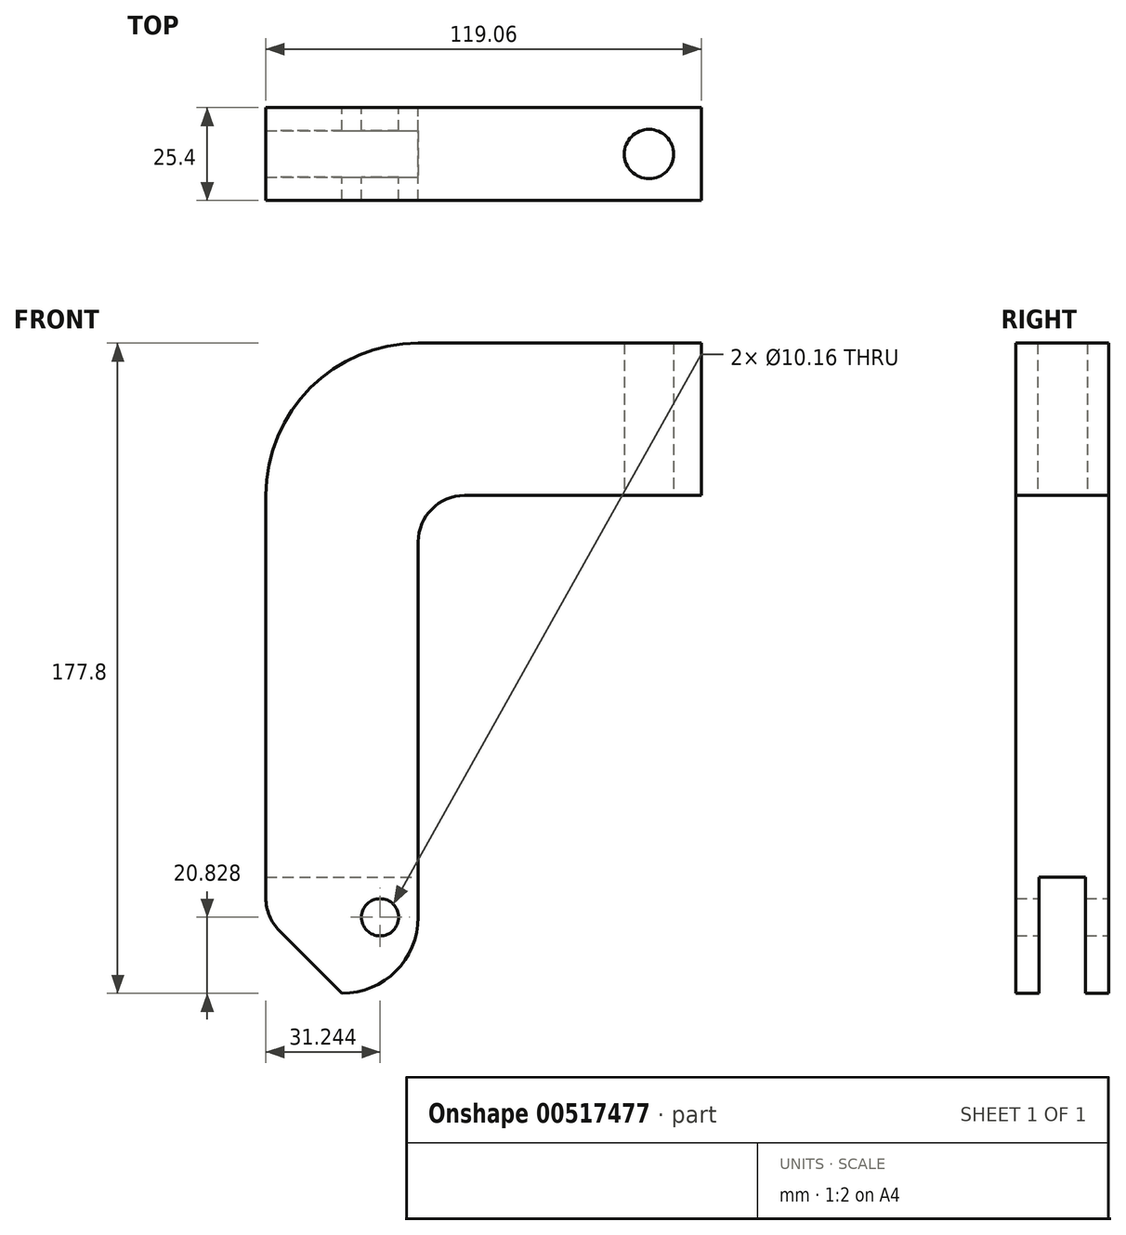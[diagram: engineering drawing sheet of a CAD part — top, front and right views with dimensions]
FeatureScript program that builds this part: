
annotation { "Feature Type Name" : "Feature", "Feature Type Description" : "" }
export const myFeature = defineFeature(function(context is Context, id is Id, definition is map)
    precondition{}
    {
        {
            var Q0;
            Q0=qCreatedBy(makeId("Front.planeOp"),FACE);
            var sketch = newSketch(context, id + "F0", { "sketchPlane" : qUnion([Q0])});
            skLineSegment(sketch, "E0.bottom", {"start": v(20.83, 88.9) * mm, "end": v(20.83, 88.9) * mm});
            skLineSegment(sketch, "E0.left", {"start": v(20.83, 34.54) * mm, "end": v(20.83, -68.07) * mm});
            skLineSegment(sketch, "E0.right", {"start": v(-20.83, 47.24) * mm, "end": v(-20.83, -62.81) * mm});
            skPoint(sketch, "E0.middle", {"position": v(0, 0) * mm});
            skPoint(sketch, "E1.visualSharp", {"position": v(-20.83, 88.9) * mm});
            skArc(sketch, "E1.filletArc", {"start": v(20.83, 88.9) * mm, "mid": v(-8.63, 76.7) * mm, "end": v(-20.83, 47.24) * mm});
            skLineSegment(sketch, "E2", {"start": v(0, -88.9) * mm, "end": v(-17.1, -71.8) * mm});
            skPoint(sketch, "E3.visualSharp", {"position": v(20.83, -88.9) * mm});
            skArc(sketch, "E3.filletArc", {"start": v(0, -88.9) * mm, "mid": v(14.73, -82.8) * mm, "end": v(20.83, -68.07) * mm});
            skPoint(sketch, "E0.top.end.orphan", {"position": v(-20.83, -88.9) * mm});
            skLineSegment(sketch, "E4", {"start": v(33.53, 47.24) * mm, "end": v(98.23, 47.24) * mm});
            skLineSegment(sketch, "E5", {"start": v(20.83, 88.9) * mm, "end": v(98.23, 88.9) * mm});
            skLineSegment(sketch, "E6", {"start": v(98.23, 88.9) * mm, "end": v(98.23, 47.24) * mm});
            skPoint(sketch, "E7.visualSharp", {"position": v(-20.83, -68.07) * mm});
            skArc(sketch, "E7.filletArc", {"start": v(-20.83, -62.81) * mm, "mid": v(-19.86, -67.67) * mm, "end": v(-17.1, -71.8) * mm});
            skArc(sketch, "E8.filletArc", {"start": v(33.53, 47.24) * mm, "mid": v(24.55, 43.52) * mm, "end": v(20.83, 34.54) * mm});
            skCircle(sketch, "E9", {"center": v(10.41, -68.07) * mm, "radius": 5.08 * mm});
            skPoint(sketch, "E10.end.orphan", {"position": v(15.5, -68.07) * mm});
            skSolve(sketch);
        }
        {
            var Q0;
            Q0 = qSketchRegion(id + "F0", true);
            extrude(context, id + "F1", {"entities" : qUnion([Q0]), "endBound" : BoundingType.SYMMETRIC, "depth" : 25.4 * mm, "offsetDistance" : 25.4 * mm});
        }
        {
            var Q0;
            Q0=qCreatedBy(makeId("Top.planeOp"),FACE);
            var sketch = newSketch(context, id + "F2", { "sketchPlane" : qUnion([Q0])});
            skPoint(sketch, "E11", {"position": v(83.95, 0) * mm});
            skSolve(sketch);
        }
        {
            var Q0;
            Q0=sQuery(id+"F2.wireOp",VERTEX,"E11");
            var Q1;
            Q1=makeQuery(id+"F1.opExtrude","SWEPT_BODY",BODY,{"disambiguationData":[OSD([sQuery(id+"F0.wireOp",EDGE,"E0.left"),sQuery(id+"F0.wireOp",EDGE,"E0.right"),sQuery(id+"F0.wireOp",EDGE,"E1.filletArc"),sQuery(id+"F0.wireOp",EDGE,"E2"),sQuery(id+"F0.wireOp",EDGE,"E3.filletArc"),sQuery(id+"F0.wireOp",EDGE,"E4"),sQuery(id+"F0.wireOp",EDGE,"E5"),sQuery(id+"F0.wireOp",EDGE,"E6"),sQuery(id+"F0.wireOp",EDGE,"E7.filletArc"),sQuery(id+"F0.wireOp",EDGE,"E8.filletArc"),sQuery(id+"F0.wireOp",EDGE,"E9")])]});
            hole(context, id + "F3", {"style" : HoleStyle.SIMPLE, "endStyle" : HoleEndStyle.THROUGH, "oppositeDirection" : true, "holeDiameter" : 13.5 * mm, "isTappedThrough" : true, "tappedDepth" : 12.7 * mm, "tapClearance" : 3, "locations" : qUnion([Q0]), "scope" : qUnion([Q1])});
        }
        {
            var Q0;
            Q0=qCreatedBy(makeId("Right.planeOp"),FACE);
            var sketch = newSketch(context, id + "F4", { "sketchPlane" : qUnion([Q0])});
            skLineSegment(sketch, "E12", {"start": v(0, -57.15) * mm, "end": v(0, -88.9) * mm});
            skLineSegment(sketch, "E13", {"start": v(0, -88.9) * mm, "end": v(-6.35, -88.9) * mm});
            skLineSegment(sketch, "E14", {"start": v(0, -88.9) * mm, "end": v(6.35, -88.9) * mm});
            skLineSegment(sketch, "E15", {"start": v(0, -57.15) * mm, "end": v(-6.35, -57.15) * mm});
            skLineSegment(sketch, "E16", {"start": v(0, -57.15) * mm, "end": v(6.35, -57.15) * mm});
            skLineSegment(sketch, "E17", {"start": v(-6.35, -57.15) * mm, "end": v(-6.35, -88.9) * mm});
            skLineSegment(sketch, "E18", {"start": v(6.35, -57.15) * mm, "end": v(6.35, -88.9) * mm});
            skSolve(sketch);
        }
        {
            var Q0;
            Q0 = qSketchRegion(id + "F4", true);
            extrude(context, id + "F5", {"entities" : qUnion([Q0]), "operationType" : NewBodyOperationType.REMOVE, "endBound" : BoundingType.SYMMETRIC, "oppositeDirection" : true, "depth" : 101.6 * mm, "offsetDistance" : 25.4 * mm});
        }
    });
